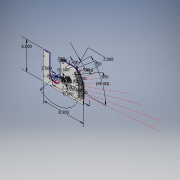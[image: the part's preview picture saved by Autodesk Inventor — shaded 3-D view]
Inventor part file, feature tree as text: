
AUTODESK INVENTOR PART (.ipt)
format: ipt  version: 2018 (Build 220112000, 112)  size: 279,552 bytes
history: native  units: in
note: dims shown in document units (in); Inventor stores cm internally (conversion verified against a paired STEP export)
features: sketch x2, extrude x2
ambient origin geometry x8: Origin, YZ Plane, XZ Plane, XY Plane, X Axis, Y Axis, Z Axis, Center Point
bodies: Solid1 (feature_tree)
feature tree (4):
  sketch  "Sketch1"  dims[d1=1.2in d2=8.5in]
  extrude  "Extrusion1"  Depth=8.5in
  extrude  "Extrusion2"  Depth=2.2in
  sketch  "Sketch2"  dims[d3=6.0in d4=2.2in d5=0.0in d6=0.0344in d7=0.0687in d8=15.0deg d9=0.1374in d10=45.0deg d11=2.5in d12=0.1718in d13=0.2405in d14=30.0deg d15=0.2749in d16=45.0deg d19=0.95in d21=0.0in d22=10.5in d23=0.95in d26=0.95in d28=0.95in d30=0.95in d32=0.95in d34=0.95in d36=0.95in d38=0.95in d39=0.95in d41=8.0in d42=0.135in d43=0.135in d44=0.135in d45=0.135in d46=0.135in d47=0.135in d48=0.135in d49=0.135in d50=0.135in d51=0.135in d52=0.135in d53=0.135in d54=0.135in d55=0.135in d56=0.135in d57=0.135in d58=0.135in d59=0.135in d60=0.135in d61=0.135in d62=2.0in d63=0.1in d64=0.0in d65=0.15in d66=0.3in d67=1.0in d68=0.3in d69=1.0in d70=0.15in d71=0.3in d72=1.5in d73=0.3in d74=0.15in d75=1.5in d76=0.3in d77=0.15in d78=1.5in d79=0.3in d80=0.15in d81=2.3in d82=2.4in d83=0.3in d84=0.15in d85=0.05in d86=0.3in d87=0.15in d88=0.5in d89=0.15in d90=1.0in d91=0.0in]
